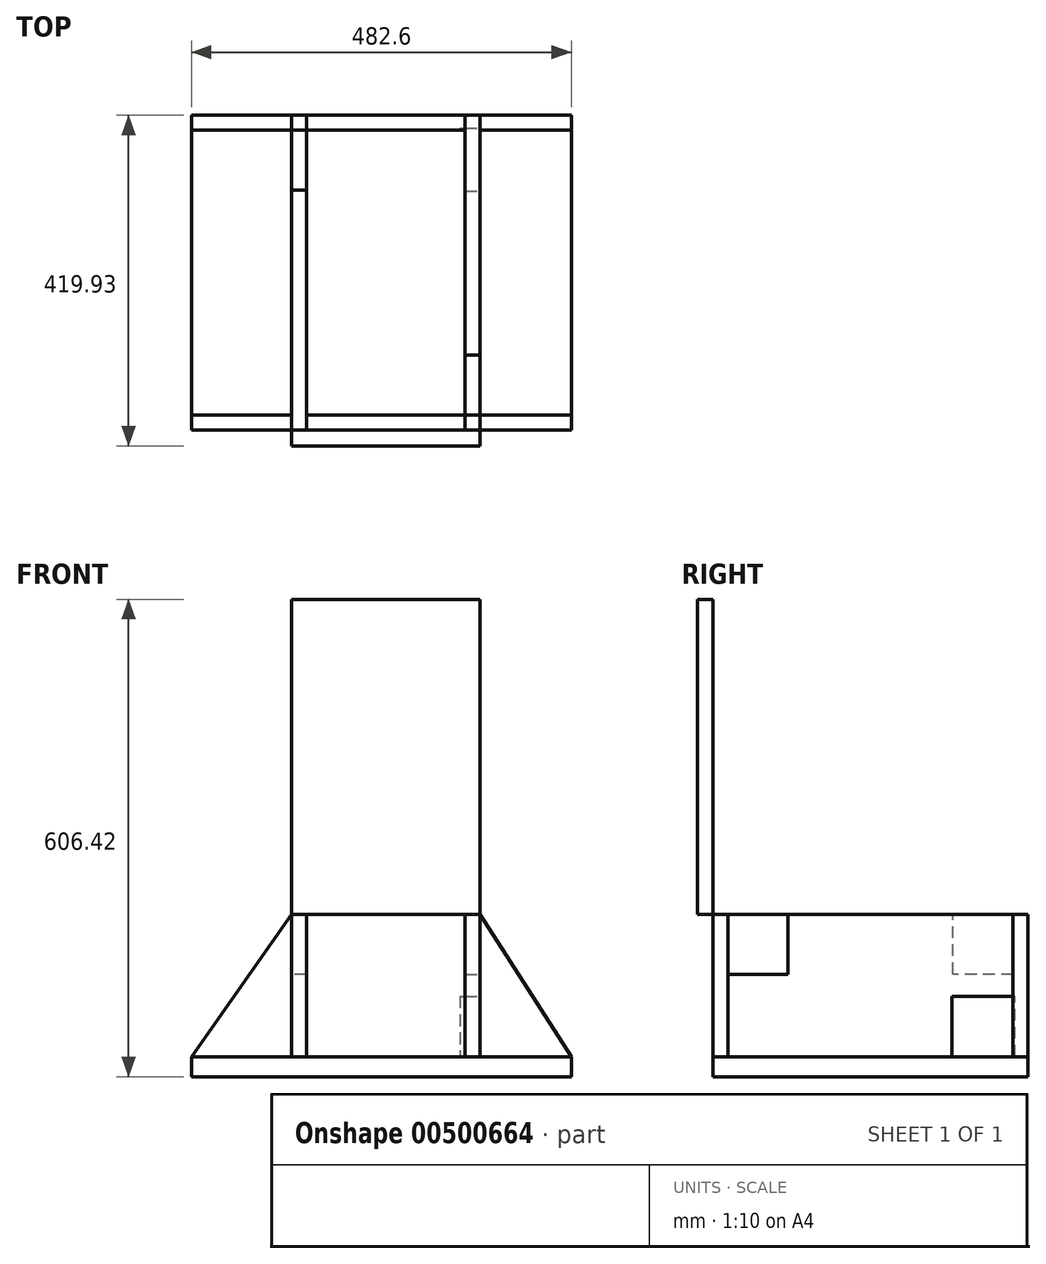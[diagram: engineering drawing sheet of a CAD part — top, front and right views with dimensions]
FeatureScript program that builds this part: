
annotation { "Feature Type Name" : "Feature", "Feature Type Description" : "" }
export const myFeature = defineFeature(function(context is Context, id is Id, definition is map)
    precondition{}
    {
        {
            var Q0;
            Q0=qCreatedBy(makeId("Top.planeOp"),FACE);
            var sketch = newSketch(context, id + "F0", { "sketchPlane" : qUnion([Q0])});
            skLineSegment(sketch, "E0.bottom", {"start": v(-253.76, 241.53) * mm, "end": v(228.84, 241.53) * mm});
            skLineSegment(sketch, "E0.top", {"start": v(-253.76, -158.52) * mm, "end": v(228.84, -158.52) * mm});
            skLineSegment(sketch, "E0.left", {"start": v(-253.76, 241.53) * mm, "end": v(-253.76, -158.52) * mm});
            skLineSegment(sketch, "E0.right", {"start": v(228.84, 241.53) * mm, "end": v(228.84, -158.52) * mm});
            skSolve(sketch);
        }
        {
            var Q0;
            Q0=makeQuery(id+"F0.imprint","IMPRINT",FACE,{"disambiguationData":[TD([[makeQuery(id+"F0.imprint","IMPRINT",EDGE,{"derivedFrom":sQuery(id+"F0.wireOp",EDGE,"E0.bottom")}),-1.0]])]});
            extrude(context, id + "F1", {"entities" : qUnion([Q0]), "depth" : 25.4 * mm, "offsetDistance" : 25.4 * mm});
        }
        {
            var Q0;
            Q0=makeQuery(id+"F1.opExtrude","CAP_FACE",FACE,{"disambiguationData":[OSD([sQuery(id+"F0.wireOp",EDGE,"E0.bottom"),sQuery(id+"F0.wireOp",EDGE,"E0.top"),sQuery(id+"F0.wireOp",EDGE,"E0.left"),sQuery(id+"F0.wireOp",EDGE,"E0.right")])],"isStart":false});
            var sketch = newSketch(context, id + "F2", { "sketchPlane" : qUnion([Q0])});
            skLineSegment(sketch, "E1.bottom", {"start": v(-126.76, 241.53) * mm, "end": v(-107.7, 241.53) * mm});
            skLineSegment(sketch, "E1.top", {"start": v(-126.76, -158.52) * mm, "end": v(-107.7, -158.52) * mm});
            skLineSegment(sketch, "E1.left", {"start": v(-126.76, 241.53) * mm, "end": v(-126.76, -158.52) * mm});
            skLineSegment(sketch, "E1.right", {"start": v(-107.7, 241.53) * mm, "end": v(-107.7, -158.52) * mm});
            skLineSegment(sketch, "E2.bottom", {"start": v(93.94, 241.53) * mm, "end": v(112.99, 241.53) * mm});
            skLineSegment(sketch, "E2.top", {"start": v(93.94, -158.52) * mm, "end": v(112.99, -158.52) * mm});
            skLineSegment(sketch, "E2.left", {"start": v(93.94, 241.53) * mm, "end": v(93.94, -158.52) * mm});
            skLineSegment(sketch, "E2.right", {"start": v(112.99, 241.53) * mm, "end": v(112.99, -158.52) * mm});
            skLineSegment(sketch, "E3.bottom", {"start": v(-107.7, 241.53) * mm, "end": v(93.94, 241.53) * mm});
            skLineSegment(sketch, "E3.top", {"start": v(-107.7, 222.48) * mm, "end": v(93.94, 222.48) * mm});
            skLineSegment(sketch, "E3.left", {"start": v(-107.7, 241.53) * mm, "end": v(-107.7, 222.48) * mm});
            skLineSegment(sketch, "E3.right", {"start": v(93.94, 241.53) * mm, "end": v(93.94, 222.48) * mm});
            skLineSegment(sketch, "E4.bottom", {"start": v(-107.7, -158.52) * mm, "end": v(93.94, -158.52) * mm});
            skLineSegment(sketch, "E4.top", {"start": v(-107.7, -139.47) * mm, "end": v(93.94, -139.47) * mm});
            skLineSegment(sketch, "E4.left", {"start": v(-107.7, -158.52) * mm, "end": v(-107.7, -139.47) * mm});
            skLineSegment(sketch, "E4.right", {"start": v(93.94, -158.52) * mm, "end": v(93.94, -139.47) * mm});
            skLineSegment(sketch, "E5.bottom", {"start": v(-21.45, 222.48) * mm, "end": v(-2.4, 222.48) * mm});
            skLineSegment(sketch, "E5.top", {"start": v(-21.45, -139.47) * mm, "end": v(-2.4, -139.47) * mm});
            skLineSegment(sketch, "E5.left", {"start": v(-21.45, 222.48) * mm, "end": v(-21.45, -139.47) * mm});
            skLineSegment(sketch, "E5.right", {"start": v(-2.4, 222.48) * mm, "end": v(-2.4, -139.47) * mm});
            skLineSegment(sketch, "E6.bottom", {"start": v(-253.76, 241.53) * mm, "end": v(-126.76, 241.53) * mm});
            skLineSegment(sketch, "E6.top", {"start": v(-253.76, 222.48) * mm, "end": v(-126.76, 222.48) * mm});
            skLineSegment(sketch, "E6.left", {"start": v(-253.76, 241.53) * mm, "end": v(-253.76, 222.48) * mm});
            skLineSegment(sketch, "E6.right", {"start": v(-126.76, 241.53) * mm, "end": v(-126.76, 222.48) * mm});
            skLineSegment(sketch, "E7.bottom", {"start": v(112.99, 241.53) * mm, "end": v(228.84, 241.53) * mm});
            skLineSegment(sketch, "E7.top", {"start": v(112.99, 222.48) * mm, "end": v(228.84, 222.48) * mm});
            skLineSegment(sketch, "E7.left", {"start": v(112.99, 241.53) * mm, "end": v(112.99, 222.48) * mm});
            skLineSegment(sketch, "E7.right", {"start": v(228.84, 241.53) * mm, "end": v(228.84, 222.48) * mm});
            skLineSegment(sketch, "E8.bottom", {"start": v(-126.76, -158.52) * mm, "end": v(-253.76, -158.52) * mm});
            skLineSegment(sketch, "E8.top", {"start": v(-126.76, -139.47) * mm, "end": v(-253.76, -139.47) * mm});
            skLineSegment(sketch, "E8.left", {"start": v(-126.76, -158.52) * mm, "end": v(-126.76, -139.47) * mm});
            skLineSegment(sketch, "E8.right", {"start": v(-253.76, -158.52) * mm, "end": v(-253.76, -139.47) * mm});
            skLineSegment(sketch, "E9.bottom", {"start": v(112.99, -139.47) * mm, "end": v(228.84, -139.47) * mm});
            skLineSegment(sketch, "E9.top", {"start": v(112.99, -158.52) * mm, "end": v(228.84, -158.52) * mm});
            skLineSegment(sketch, "E9.left", {"start": v(112.99, -139.47) * mm, "end": v(112.99, -158.52) * mm});
            skLineSegment(sketch, "E9.right", {"start": v(228.84, -139.47) * mm, "end": v(228.84, -158.52) * mm});
            skSolve(sketch);
        }
        {
            var Q0;
            Q0=makeQuery(id+"F2.imprint","IMPRINT",FACE,{"disambiguationData":[TD([[makeQuery(id+"F2.imprint","IMPRINT",EDGE,{"derivedFrom":sQuery(id+"F2.wireOp",EDGE,"E1.bottom")}),-1.0]])]});
            var Q1;
            Q1=makeQuery(id+"F2.imprint","IMPRINT",FACE,{"disambiguationData":[TD([[makeQuery(id+"F2.imprint","IMPRINT",EDGE,{"derivedFrom":sQuery(id+"F2.wireOp",EDGE,"E5.bottom")}),-1.0]])]});
            var Q2;
            Q2=makeQuery(id+"F2.imprint","IMPRINT",FACE,{"disambiguationData":[TD([[makeQuery(id+"F2.imprint","IMPRINT",EDGE,{"derivedFrom":sQuery(id+"F2.wireOp",EDGE,"E2.bottom")}),-1.0]])]});
            extrude(context, id + "F3", {"entities" : qUnion([Q0, Q1, Q2]), "depth" : 180.97 * mm, "offsetDistance" : 25.4 * mm});
        }
        {
            var Q0;
            Q0=makeQuery(id+"F2.imprint","IMPRINT",FACE,{"disambiguationData":[TD([[makeQuery(id+"F2.imprint","IMPRINT",EDGE,{"derivedFrom":sQuery(id+"F2.wireOp",EDGE,"E8.bottom")}),1.0]])]});
            var Q1;
            Q1=makeQuery(id+"F2.imprint","IMPRINT",FACE,{"disambiguationData":[TD([[makeQuery(id+"F2.imprint","IMPRINT",EDGE,{"derivedFrom":sQuery(id+"F2.wireOp",EDGE,"E4.bottom")}),1.0]])]});
            var Q2;
            Q2=makeQuery(id+"F2.imprint","IMPRINT",FACE,{"disambiguationData":[TD([[makeQuery(id+"F2.imprint","IMPRINT",EDGE,{"derivedFrom":sQuery(id+"F2.wireOp",EDGE,"E9.bottom")}),-1.0]])]});
            var Q3;
            Q3=makeQuery(id+"F2.imprint","IMPRINT",FACE,{"disambiguationData":[TD([[makeQuery(id+"F2.imprint","IMPRINT",EDGE,{"derivedFrom":sQuery(id+"F2.wireOp",EDGE,"E3.bottom")}),-1.0]])]});
            var Q4;
            Q4=makeQuery(id+"F2.imprint","IMPRINT",FACE,{"disambiguationData":[TD([[makeQuery(id+"F2.imprint","IMPRINT",EDGE,{"derivedFrom":sQuery(id+"F2.wireOp",EDGE,"E7.bottom")}),-1.0]])]});
            var Q5;
            Q5=makeQuery(id+"F2.imprint","IMPRINT",FACE,{"disambiguationData":[TD([[makeQuery(id+"F2.imprint","IMPRINT",EDGE,{"derivedFrom":sQuery(id+"F2.wireOp",EDGE,"E6.bottom")}),-1.0]])]});
            extrude(context, id + "F4", {"entities" : qUnion([Q0, Q1, Q2, Q3, Q4, Q5]), "depth" : 180.97 * mm, "offsetDistance" : 25.4 * mm});
        }
        {
            var Q0;
            Q0=makeQuery(id+"F4.opExtrude","SWEPT_FACE",FACE,{"disambiguationData":[OSD([sQuery(id+"F2.wireOp",EDGE,"E8.bottom")])]});
            var sketch = newSketch(context, id + "F5", { "sketchPlane" : qUnion([Q0])});
            skLineSegment(sketch, "E10", {"start": v(-253.76, 25.4) * mm, "end": v(-126.76, 206.38) * mm});
            skSolve(sketch);
        }
        {
            var Q0;
            Q0=makeQuery(id+"F5.imprint","IMPRINT",FACE,{"disambiguationData":[TD([[makeQuery(id+"F5.imprint","IMPRINT",EDGE,{"derivedFrom":sQuery(id+"F5.wireOp",EDGE,"E10")}),1.0]])]});
            extrude(context, id + "F6", {"entities" : qUnion([Q0]), "operationType" : NewBodyOperationType.REMOVE, "endBound" : BoundingType.THROUGH_ALL, "oppositeDirection" : true, "depth" : 25.4 * mm, "offsetDistance" : 25.4 * mm});
        }
        {
            var Q0;
            Q0=makeQuery(id+"F4.opExtrude","SWEPT_FACE",FACE,{"disambiguationData":[OSD([sQuery(id+"F2.wireOp",EDGE,"E9.top")])]});
            var sketch = newSketch(context, id + "F7", { "sketchPlane" : qUnion([Q0])});
            skLineSegment(sketch, "E11", {"start": v(228.84, 25.4) * mm, "end": v(112.99, 206.38) * mm});
            skSolve(sketch);
        }
        {
            var Q0;
            Q0=makeQuery(id+"F7.imprint","IMPRINT",FACE,{"disambiguationData":[TD([[makeQuery(id+"F7.imprint","IMPRINT",EDGE,{"derivedFrom":sQuery(id+"F7.wireOp",EDGE,"E11")}),-1.0]])]});
            extrude(context, id + "F8", {"entities" : qUnion([Q0]), "operationType" : NewBodyOperationType.REMOVE, "endBound" : BoundingType.THROUGH_ALL, "oppositeDirection" : true, "depth" : 25.4 * mm, "offsetDistance" : 25.4 * mm});
        }
        {
            var Q0;
            Q0=makeQuery(id+"F3.opExtrude","CAP_FACE",FACE,{"disambiguationData":[OSD([sQuery(id+"F2.wireOp",EDGE,"E1.bottom"),sQuery(id+"F2.wireOp",EDGE,"E1.top"),sQuery(id+"F2.wireOp",EDGE,"E1.left"),sQuery(id+"F2.wireOp",EDGE,"E1.right"),sQuery(id+"F2.wireOp",EDGE,"E3.left"),sQuery(id+"F2.wireOp",EDGE,"E4.left"),sQuery(id+"F2.wireOp",EDGE,"E6.right"),sQuery(id+"F2.wireOp",EDGE,"E8.left")])],"isStart":false});
            var sketch = newSketch(context, id + "F9", { "sketchPlane" : qUnion([Q0])});
            skLineSegment(sketch, "E12.bottom", {"start": v(-126.76, -158.52) * mm, "end": v(113, -158.52) * mm});
            skLineSegment(sketch, "E12.top", {"start": v(-126.76, -178.4) * mm, "end": v(113, -178.4) * mm});
            skLineSegment(sketch, "E12.left", {"start": v(-126.76, -178.4) * mm, "end": v(-126.76, -158.52) * mm});
            skLineSegment(sketch, "E12.right", {"start": v(113, -178.4) * mm, "end": v(113, -158.52) * mm});
            skSolve(sketch);
        }
        {
            var Q0;
            Q0 = qSketchRegion(id + "F9", true);
            extrude(context, id + "F10", {"entities" : qUnion([Q0]), "depth" : 400.05 * mm, "offsetDistance" : 25.4 * mm});
        }
        {
            var Q0;
            Q0=makeQuery(id+"F4.opExtrude","CAP_FACE",FACE,{"disambiguationData":[OSD([sQuery(id+"F2.wireOp",EDGE,"E4.bottom"),sQuery(id+"F2.wireOp",EDGE,"E4.top"),sQuery(id+"F2.wireOp",EDGE,"E4.left"),sQuery(id+"F2.wireOp",EDGE,"E4.right"),sQuery(id+"F2.wireOp",EDGE,"E5.top")])],"isStart":false});
            var sketch = newSketch(context, id + "F11", { "sketchPlane" : qUnion([Q0])});
            skLineSegment(sketch, "E13.bottom", {"start": v(93.94, -139.47) * mm, "end": v(112.99, -139.47) * mm});
            skLineSegment(sketch, "E13.top", {"start": v(93.94, -63.27) * mm, "end": v(112.99, -63.27) * mm});
            skLineSegment(sketch, "E13.left", {"start": v(93.94, -139.47) * mm, "end": v(93.94, -63.27) * mm});
            skLineSegment(sketch, "E13.right", {"start": v(112.99, -139.47) * mm, "end": v(112.99, -63.27) * mm});
            skSolve(sketch);
        }
        {
            var Q0;
            Q0 = qSketchRegion(id + "F11", true);
            extrude(context, id + "F12", {"entities" : qUnion([Q0]), "operationType" : NewBodyOperationType.REMOVE, "oppositeDirection" : true, "depth" : 76.2 * mm, "offsetDistance" : 25.4 * mm});
        }
        {
            var Q0;
            Q0=makeQuery(id+"F3.opExtrude","SWEPT_FACE",FACE,{"disambiguationData":[OSD([sQuery(id+"F2.wireOp",EDGE,"E2.right"),sQuery(id+"F2.wireOp",EDGE,"E7.left"),sQuery(id+"F2.wireOp",EDGE,"E9.left")])]});
            var sketch = newSketch(context, id + "F13", { "sketchPlane" : qUnion([Q0])});
            skLineSegment(sketch, "E14.bottom", {"start": v(225.14, 25.4) * mm, "end": v(145.07, 25.4) * mm});
            skLineSegment(sketch, "E14.top", {"start": v(225.14, 102.15) * mm, "end": v(145.07, 102.15) * mm});
            skLineSegment(sketch, "E14.left", {"start": v(225.14, 25.4) * mm, "end": v(225.14, 102.15) * mm});
            skLineSegment(sketch, "E14.right", {"start": v(145.07, 25.4) * mm, "end": v(145.07, 102.15) * mm});
            skSolve(sketch);
        }
        {
            var Q0;
            Q0 = qSketchRegion(id + "F13", true);
            extrude(context, id + "F14", {"entities" : qUnion([Q0]), "operationType" : NewBodyOperationType.REMOVE, "oppositeDirection" : true, "depth" : 25.4 * mm, "offsetDistance" : 25.4 * mm});
        }
        {
            var Q0;
            Q0=makeQuery(id+"F4.opExtrude","CAP_FACE",FACE,{"disambiguationData":[OSD([sQuery(id+"F2.wireOp",EDGE,"E3.bottom"),sQuery(id+"F2.wireOp",EDGE,"E3.top"),sQuery(id+"F2.wireOp",EDGE,"E3.left"),sQuery(id+"F2.wireOp",EDGE,"E3.right"),sQuery(id+"F2.wireOp",EDGE,"E5.bottom")])],"isStart":false});
            var sketch = newSketch(context, id + "F15", { "sketchPlane" : qUnion([Q0])});
            skLineSegment(sketch, "E15.bottom", {"start": v(-107.7, 222.48) * mm, "end": v(-133.1, 222.48) * mm});
            skLineSegment(sketch, "E15.top", {"start": v(-107.7, 146.28) * mm, "end": v(-133.1, 146.28) * mm});
            skLineSegment(sketch, "E15.left", {"start": v(-107.7, 222.48) * mm, "end": v(-107.7, 146.28) * mm});
            skLineSegment(sketch, "E15.right", {"start": v(-133.1, 222.48) * mm, "end": v(-133.1, 146.28) * mm});
            skSolve(sketch);
        }
        {
            var Q0;
            Q0 = qSketchRegion(id + "F15", true);
            extrude(context, id + "F16", {"entities" : qUnion([Q0]), "operationType" : NewBodyOperationType.REMOVE, "oppositeDirection" : true, "depth" : 76.2 * mm, "offsetDistance" : 25.4 * mm});
        }
    });
